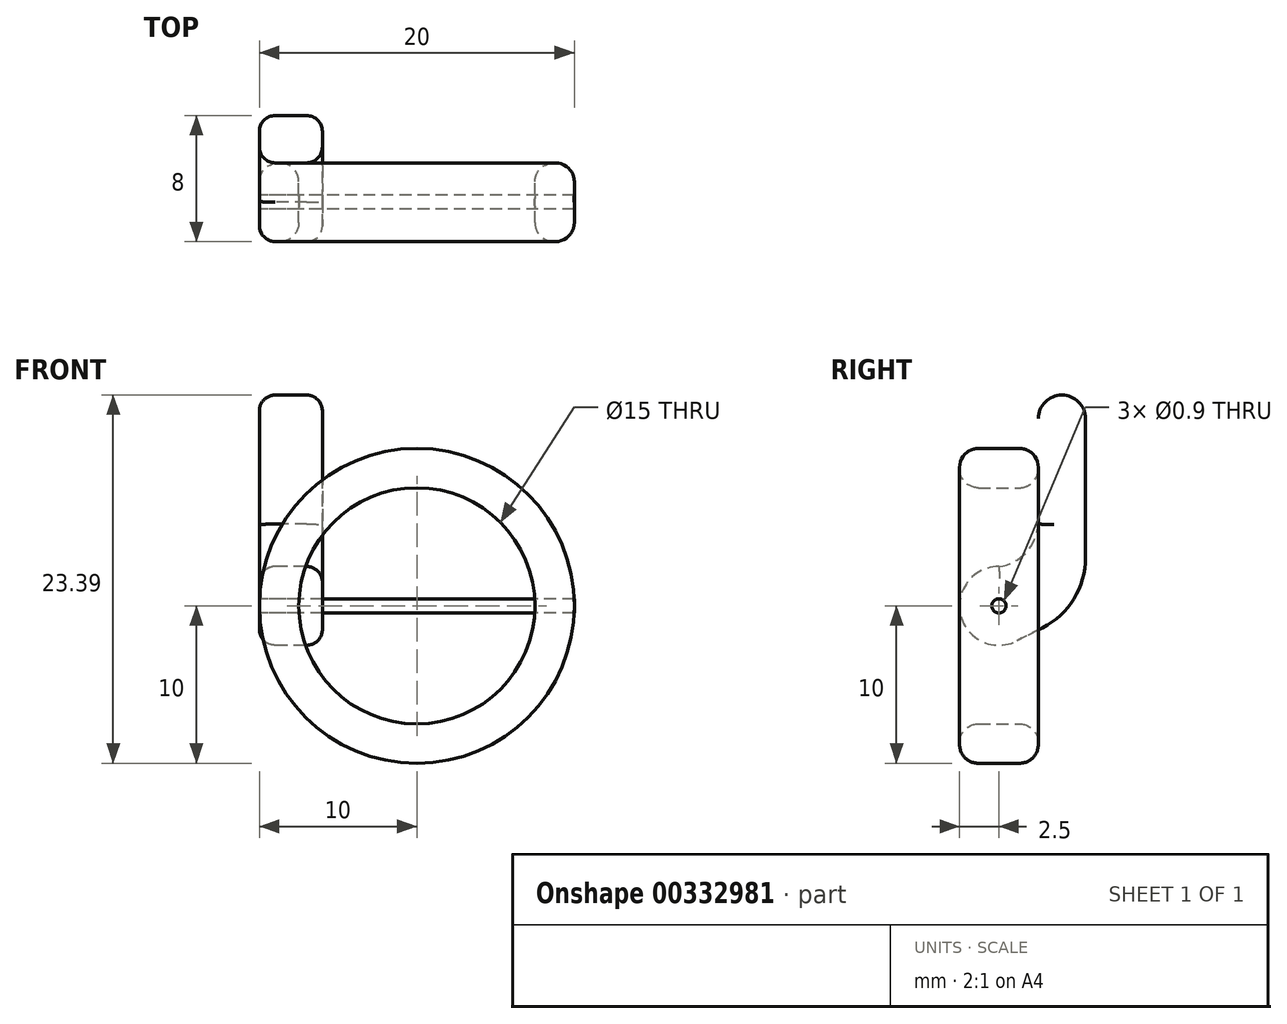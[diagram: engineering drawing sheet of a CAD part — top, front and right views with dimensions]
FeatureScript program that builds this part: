
annotation { "Feature Type Name" : "Feature", "Feature Type Description" : "" }
export const myFeature = defineFeature(function(context is Context, id is Id, definition is map)
    precondition{}
    {
        {
            var Q0;
            Q0=qCreatedBy(makeId("Right.planeOp"),FACE);
            var sketch = newSketch(context, id + "F0", { "sketchPlane" : qUnion([Q0])});
            skCircle(sketch, "E0", {"center": v(0, 0) * mm, "radius": 0.45 * mm});
            skSolve(sketch);
        }
        {
            var Q0;
            Q0=makeQuery(id+"F0.imprint","IMPRINT",FACE,{"disambiguationData":[TD([[makeQuery(id+"F0.imprint","IMPRINT",EDGE,{"derivedFrom":sQuery(id+"F0.wireOp",EDGE,"E0")}),1.0]])]});
            extrude(context, id + "F1", {"entities" : qUnion([Q0]), "depth" : 20 * mm});
        }
        {
            var Q0;
            Q0=qCreatedBy(makeId("Front.planeOp"),FACE);
            var sketch = newSketch(context, id + "F2", { "sketchPlane" : qUnion([Q0])});
            skCircle(sketch, "E1", {"center": v(10, 0) * mm, "radius": 10 * mm});
            skLineSegment(sketch, "E2", {"start": v(10, 0) * mm, "end": v(0, 0) * mm, "construction": true});
            skLineSegment(sketch, "E3", {"start": v(0, 0) * mm, "end": v(10, 0) * mm, "construction": true});
            skLineSegment(sketch, "E4", {"start": v(10, 0) * mm, "end": v(20, 0) * mm, "construction": true});
            skLineSegment(sketch, "E5", {"start": v(20, 0) * mm, "end": v(10, 0) * mm, "construction": true});
            skCircle(sketch, "E6", {"center": v(10, 0) * mm, "radius": 7.5 * mm});
            skSolve(sketch);
        }
        {
            var Q0;
            Q0 = qSketchRegion(id + "F2", true);
            extrude(context, id + "F3", {"entities" : qUnion([Q0]), "endBound" : BoundingType.SYMMETRIC, "depth" : 5 * mm});
        }
        {
            var Q0;
            Q0=makeQuery(id+"F3.opExtrude","CAP_FACE",FACE,{"disambiguationData":[OSD([sQuery(id+"F2.wireOp",EDGE,"E1"),sQuery(id+"F2.wireOp",EDGE,"E6")])],"isStart":true});
            var Q1;
            Q1=makeQuery(id+"F3.opExtrude","CAP_FACE",FACE,{"disambiguationData":[OSD([sQuery(id+"F2.wireOp",EDGE,"E1"),sQuery(id+"F2.wireOp",EDGE,"E6")])],"isStart":false});
            fillet(context, id + "F4", {"entities" : qUnion([Q0, Q1]), "radius" : 1.2 * mm, "tangentPropagation" : true, "allowEdgeOverflow" : false});
        }
        {
            var Q0;
            Q0=qCreatedBy(makeId("Right.planeOp"),FACE);
            var sketch = newSketch(context, id + "F5", { "sketchPlane" : qUnion([Q0])});
            skArc(sketch, "E7", {"start": v(0, 2.5) * mm, "mid": v(-2.43, -0.58) * mm, "end": v(1.14, -2.23) * mm});
            skLineSegment(sketch, "E8", {"start": v(2.5, 5.2) * mm, "end": v(2.5, 11.9) * mm});
            skLineSegment(sketch, "E9", {"start": v(5.5, 11.9) * mm, "end": v(5.5, 3.06) * mm});
            skLineSegment(sketch, "E10", {"start": v(2.77, -1.4) * mm, "end": v(1.14, -2.23) * mm});
            skArc(sketch, "E11", {"start": v(0, 2.5) * mm, "mid": v(1.74, 3.4) * mm, "end": v(2.5, 5.2) * mm});
            skArc(sketch, "E12", {"start": v(5.5, 11.9) * mm, "mid": v(4, 13.4) * mm, "end": v(2.5, 11.9) * mm});
            skPoint(sketch, "E13.orphan", {"position": v(2.5, 0) * mm});
            skPoint(sketch, "E14.visualSharp", {"position": v(5.5, 0) * mm});
            skArc(sketch, "E14.filletArc", {"start": v(2.77, -1.4) * mm, "mid": v(4.76, 0.45) * mm, "end": v(5.5, 3.06) * mm});
            skSolve(sketch);
        }
        {
            var Q0;
            Q0 = qSketchRegion(id + "F5", true);
            extrude(context, id + "F6", {"entities" : qUnion([Q0]), "depth" : 4 * mm});
        }
        {
            var Q0;
            Q0=makeQuery(id+"F6.opExtrude","CAP_FACE",FACE,{"disambiguationData":[OSD([sQuery(id+"F5.wireOp",EDGE,"E7"),sQuery(id+"F5.wireOp",EDGE,"E8"),sQuery(id+"F5.wireOp",EDGE,"E9"),sQuery(id+"F5.wireOp",EDGE,"E10"),sQuery(id+"F5.wireOp",EDGE,"E11"),sQuery(id+"F5.wireOp",EDGE,"E12"),sQuery(id+"F5.wireOp",EDGE,"E14.filletArc")])],"isStart":false});
            var Q1;
            Q1=makeQuery(id+"F6.opExtrude","CAP_FACE",FACE,{"disambiguationData":[OSD([sQuery(id+"F5.wireOp",EDGE,"E7"),sQuery(id+"F5.wireOp",EDGE,"E8"),sQuery(id+"F5.wireOp",EDGE,"E9"),sQuery(id+"F5.wireOp",EDGE,"E10"),sQuery(id+"F5.wireOp",EDGE,"E11"),sQuery(id+"F5.wireOp",EDGE,"E12"),sQuery(id+"F5.wireOp",EDGE,"E14.filletArc")])],"isStart":true});
            fillet(context, id + "F7", {"entities" : qUnion([Q0, Q1]), "radius" : 1 * mm, "tangentPropagation" : true, "allowEdgeOverflow" : false});
        }
        {
            var Q0;
            Q0=makeQuery(id+"F1.opExtrude","SWEPT_BODY",BODY,{"disambiguationData":[OSD([sQuery(id+"F0.wireOp",EDGE,"E0")])]});
            var Q1;
            Q1=makeQuery(id+"F6.opExtrude","SWEPT_BODY",BODY,{"disambiguationData":[OSD([sQuery(id+"F5.wireOp",EDGE,"E7"),sQuery(id+"F5.wireOp",EDGE,"E8"),sQuery(id+"F5.wireOp",EDGE,"E9"),sQuery(id+"F5.wireOp",EDGE,"E10"),sQuery(id+"F5.wireOp",EDGE,"E11"),sQuery(id+"F5.wireOp",EDGE,"E12"),sQuery(id+"F5.wireOp",EDGE,"E14.filletArc")])]});
            booleanBodies(context, id + "F8", {"operationType" : BooleanOperationType.SUBTRACTION, "tools" : qUnion([Q0]), "targets" : qUnion([Q1]), "keepTools" : true});
        }
        {
            var Q0;
            Q0=makeQuery(id+"F1.opExtrude","SWEPT_BODY",BODY,{"disambiguationData":[OSD([sQuery(id+"F0.wireOp",EDGE,"E0")])]});
            var Q1;
            Q1=makeQuery(id+"F3.opExtrude","SWEPT_BODY",BODY,{"disambiguationData":[OSD([sQuery(id+"F2.wireOp",EDGE,"E1"),sQuery(id+"F2.wireOp",EDGE,"E6")])]});
            booleanBodies(context, id + "F9", {"operationType" : BooleanOperationType.SUBTRACTION, "tools" : qUnion([Q0]), "targets" : qUnion([Q1]), "keepTools" : true});
        }
    });
